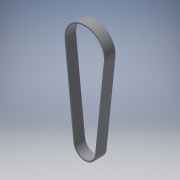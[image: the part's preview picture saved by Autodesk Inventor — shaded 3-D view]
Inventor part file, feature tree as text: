
AUTODESK INVENTOR PART (.ipt)
format: ipt  version: 2018 (Build 220112000, 112)  size: 113,152 bytes
history: native  units: mm
features: extrude x1, sketch x1
ambient origin geometry x8: Origin, YZ Plane, XZ Plane, XY Plane, X Axis, Y Axis, Z Axis, Center Point
bodies: Solid1 (feature_tree)
feature tree (2):
  extrude  "Extrusion1"  Depth=67.5mm
  sketch  "Sketch1"  dims[d0=16.0mm d1=67.5mm d2=30.0mm d3=1.0mm d4=8.0mm d5=0.0mm]
